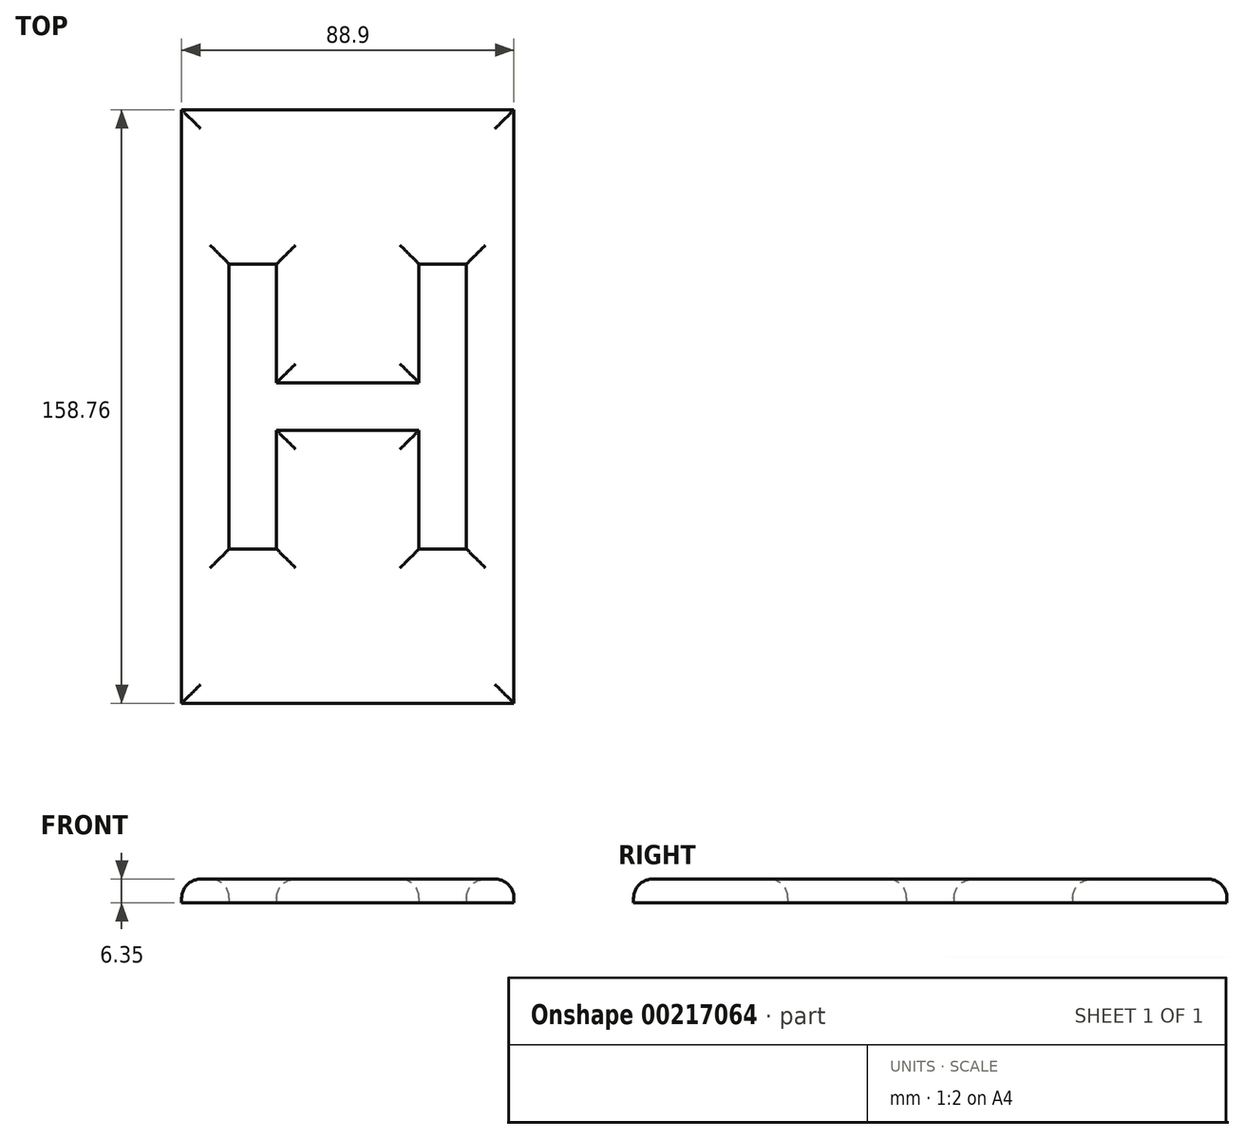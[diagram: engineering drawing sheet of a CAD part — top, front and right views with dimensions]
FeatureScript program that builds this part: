
annotation { "Feature Type Name" : "Feature", "Feature Type Description" : "" }
export const myFeature = defineFeature(function(context is Context, id is Id, definition is map)
    precondition{}
    {
        {
            var Q0;
            Q0=qCreatedBy(makeId("Top.planeOp"),FACE);
            var sketch = newSketch(context, id + "F0", { "sketchPlane" : qUnion([Q0])});
            skLineSegment(sketch, "E0.bottom", {"start": v(44.45, -79.38) * mm, "end": v(-44.45, -79.38) * mm});
            skLineSegment(sketch, "E0.top", {"start": v(44.45, 79.38) * mm, "end": v(-44.45, 79.38) * mm});
            skLineSegment(sketch, "E0.left", {"start": v(44.45, -79.38) * mm, "end": v(44.45, 79.38) * mm});
            skLineSegment(sketch, "E0.right", {"start": v(-44.45, -79.38) * mm, "end": v(-44.45, 79.38) * mm});
            skPoint(sketch, "E0.middle", {"position": v(0, 0) * mm});
            skLineSegment(sketch, "E1.bottom", {"start": v(25.4, -38.1) * mm, "end": v(19.05, -38.1) * mm});
            skLineSegment(sketch, "E1.top", {"start": v(25.4, 38.1) * mm, "end": v(19.05, 38.1) * mm});
            skLineSegment(sketch, "E2.0", {"start": v(-19.05, -38.1) * mm, "end": v(-19.05, -6.35) * mm});
            skLineSegment(sketch, "E3.0", {"start": v(19.05, -38.1) * mm, "end": v(19.05, -6.35) * mm});
            skLineSegment(sketch, "E4.0", {"start": v(-19.05, -6.35) * mm, "end": v(19.05, -6.35) * mm});
            skLineSegment(sketch, "E5.0", {"start": v(-19.05, 6.35) * mm, "end": v(19.05, 6.35) * mm});
            skLineSegment(sketch, "E6.0", {"start": v(31.75, -38.1) * mm, "end": v(31.75, 38.1) * mm});
            skLineSegment(sketch, "E7.0", {"start": v(-31.75, -38.1) * mm, "end": v(-31.75, 38.1) * mm});
            skLineSegment(sketch, "E8", {"start": v(-31.75, 38.1) * mm, "end": v(-19.05, 38.1) * mm});
            skLineSegment(sketch, "E9", {"start": v(31.75, -38.1) * mm, "end": v(25.4, -38.1) * mm});
            skLineSegment(sketch, "E10.trimOffspring", {"start": v(-19.05, 38.1) * mm, "end": v(-25.4, 38.1) * mm});
            skLineSegment(sketch, "E11.trimOffspring", {"start": v(19.05, 38.1) * mm, "end": v(31.75, 38.1) * mm});
            skLineSegment(sketch, "E12.trimOffspring", {"start": v(-19.05, -38.1) * mm, "end": v(-31.75, -38.1) * mm});
            skLineSegment(sketch, "E13.trimOffspring", {"start": v(-19.05, -38.1) * mm, "end": v(-25.4, -38.1) * mm});
            skPoint(sketch, "E14.trimOffspring.end.orphan", {"position": v(25.4, 0) * mm});
            skPoint(sketch, "E15.start.orphan", {"position": v(-25.4, 0) * mm});
            skLineSegment(sketch, "E16.trimOffspring", {"start": v(-19.05, 6.35) * mm, "end": v(-19.05, 38.1) * mm});
            skLineSegment(sketch, "E17.trimOffspring", {"start": v(19.05, 6.35) * mm, "end": v(19.05, 38.1) * mm});
            skSolve(sketch);
        }
        {
            var Q0;
            Q0=makeQuery(id+"F0.imprint","IMPRINT",FACE,{"disambiguationData":[TD([[makeQuery(id+"F0.imprint","IMPRINT",EDGE,{"derivedFrom":sQuery(id+"F0.wireOp",EDGE,"E0.bottom")}),-1.0]])]});
            extrude(context, id + "F1", {"entities" : qUnion([Q0]), "depth" : 6.35 * mm});
        }
        {
            var Q0;
            Q0=makeQuery(id+"F1.opExtrude","CAP_FACE",FACE,{"disambiguationData":[OSD([sQuery(id+"F0.wireOp",EDGE,"E0.bottom"),sQuery(id+"F0.wireOp",EDGE,"E0.top"),sQuery(id+"F0.wireOp",EDGE,"E0.left"),sQuery(id+"F0.wireOp",EDGE,"E0.right"),sQuery(id+"F0.wireOp",EDGE,"E1.bottom"),sQuery(id+"F0.wireOp",EDGE,"E2.0"),sQuery(id+"F0.wireOp",EDGE,"E3.0"),sQuery(id+"F0.wireOp",EDGE,"E4.0"),sQuery(id+"F0.wireOp",EDGE,"E5.0"),sQuery(id+"F0.wireOp",EDGE,"E6.0"),sQuery(id+"F0.wireOp",EDGE,"E7.0"),sQuery(id+"F0.wireOp",EDGE,"E8"),sQuery(id+"F0.wireOp",EDGE,"E9"),sQuery(id+"F0.wireOp",EDGE,"E10.trimOffspring"),sQuery(id+"F0.wireOp",EDGE,"E11.trimOffspring"),sQuery(id+"F0.wireOp",EDGE,"E12.trimOffspring"),sQuery(id+"F0.wireOp",EDGE,"E13.trimOffspring"),sQuery(id+"F0.wireOp",EDGE,"E16.trimOffspring"),sQuery(id+"F0.wireOp",EDGE,"E17.trimOffspring")])],"isStart":false});
            fillet(context, id + "F2", {"entities" : qUnion([Q0]), "radius" : 5.08 * mm, "tangentPropagation" : true, "allowEdgeOverflow" : false});
        }
    });
